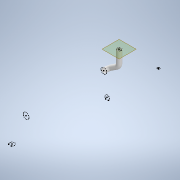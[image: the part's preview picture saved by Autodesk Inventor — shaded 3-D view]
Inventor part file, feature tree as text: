
AUTODESK INVENTOR PART (.ipt)
format: ipt  version: 2022 (Build 260153000, 153)  size: 168,960 bytes
history: native  units: mm
features: sketch x3, plane x1, sweep x1
ambient origin geometry x8: Origin, YZ Plane, XZ Plane, XY Plane, X Axis, Y Axis, Z Axis, Center Point
bodies: Solid1 (feature_tree)
feature tree (5):
  sketch  "3D Sketch1"
  sketch  "3D Sketch2"
  plane  "Work Plane1"
  sweep  "Sweep1"
  sketch  "Sketch1"  dims[d1=0.0mm d2=0.0mm d3=5.0mm d4=5.0mm]
